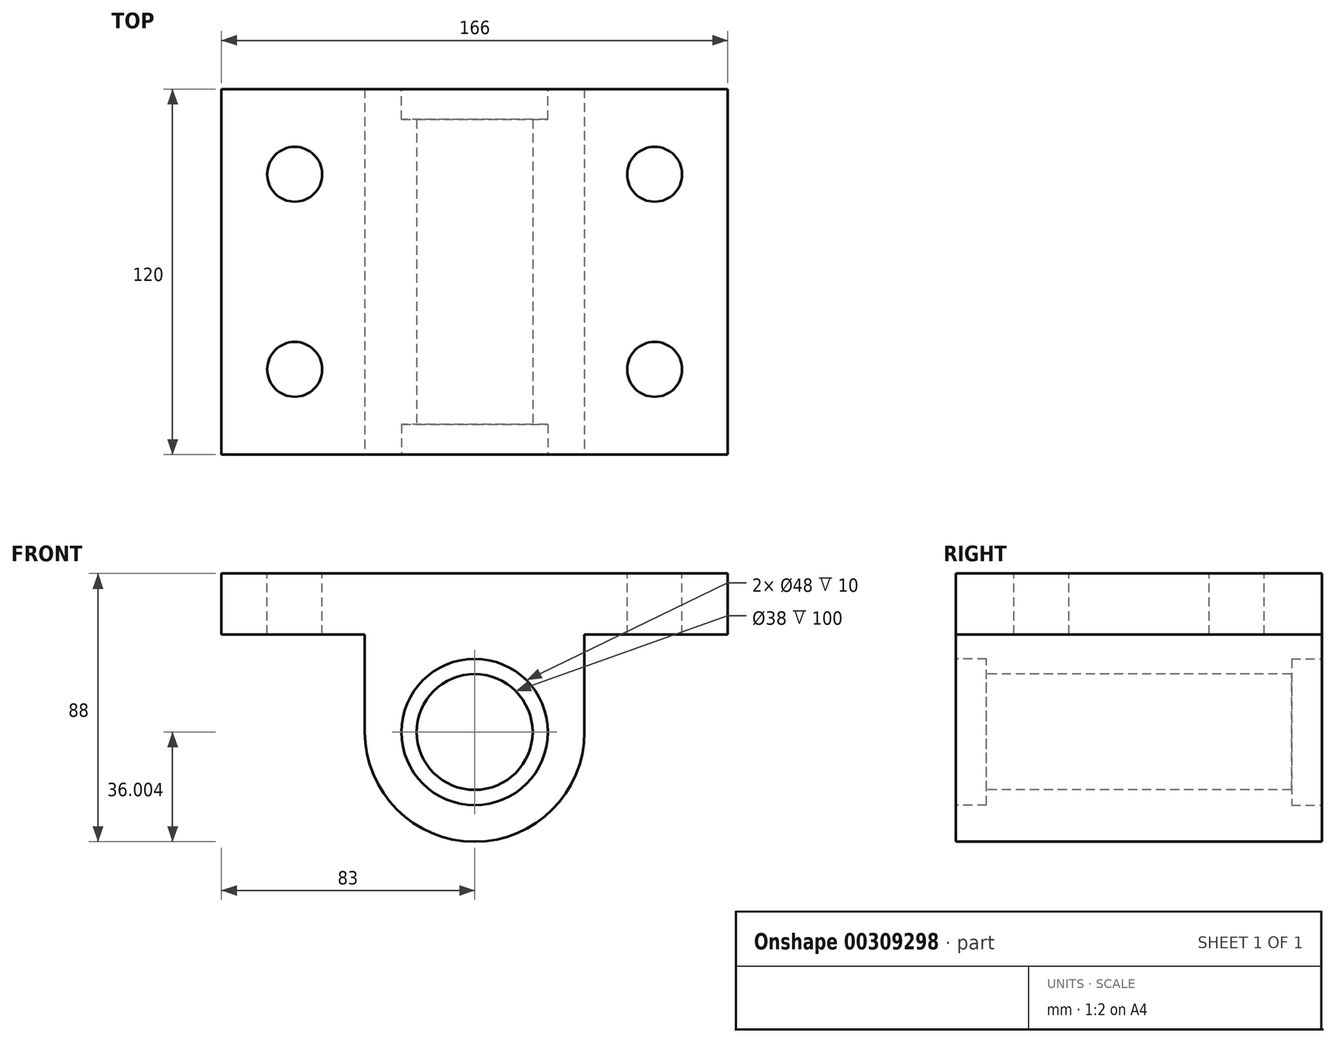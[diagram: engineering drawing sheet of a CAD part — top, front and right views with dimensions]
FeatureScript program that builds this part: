
annotation { "Feature Type Name" : "Feature", "Feature Type Description" : "" }
export const myFeature = defineFeature(function(context is Context, id is Id, definition is map)
    precondition{}
    {
        {
            var Q0;
            Q0=qCreatedBy(makeId("Front.planeOp"),FACE);
            var sketch = newSketch(context, id + "F0", { "sketchPlane" : qUnion([Q0])});
            skLineSegment(sketch, "E0.bottom", {"start": v(83, 33.32) * mm, "end": v(-83, 33.32) * mm});
            skLineSegment(sketch, "E0.top", {"start": v(83, 13.32) * mm, "end": v(36, 13.32) * mm});
            skLineSegment(sketch, "E0.left", {"start": v(83, 33.32) * mm, "end": v(83, 13.32) * mm});
            skLineSegment(sketch, "E0.right", {"start": v(-83, 33.32) * mm, "end": v(-83, 13.32) * mm});
            skPoint(sketch, "E0.middle", {"position": v(0, 23.32) * mm});
            skArc(sketch, "E1", {"start": v(-36, -18.68) * mm, "mid": v(0, -54.68) * mm, "end": v(36, -18.68) * mm});
            skCircle(sketch, "E2", {"center": v(0, -18.68) * mm, "radius": 24 * mm});
            skLineSegment(sketch, "E3", {"start": v(-36, 13.32) * mm, "end": v(-36, -18.68) * mm});
            skLineSegment(sketch, "E4", {"start": v(36, 13.32) * mm, "end": v(36, -18.68) * mm});
            skLineSegment(sketch, "E5.trimOffspring", {"start": v(-36, 13.32) * mm, "end": v(-83, 13.32) * mm});
            skCircle(sketch, "E6.0", {"center": v(0, -18.68) * mm, "radius": 19 * mm});
            skSolve(sketch);
        }
        {
            var Q0;
            Q0=makeQuery(id+"F0.imprint","IMPRINT",FACE,{"disambiguationData":[TD([[makeQuery(id+"F0.imprint","IMPRINT",EDGE,{"derivedFrom":sQuery(id+"F0.wireOp",EDGE,"E2")}),1.0]])]});
            var Q1;
            Q1=makeQuery(id+"F0.imprint","IMPRINT",FACE,{"disambiguationData":[TD([[makeQuery(id+"F0.imprint","IMPRINT",EDGE,{"derivedFrom":sQuery(id+"F0.wireOp",EDGE,"E0.bottom")}),1.0]])]});
            extrude(context, id + "F1", {"entities" : qUnion([Q0, Q1]), "endBound" : BoundingType.SYMMETRIC, "oppositeDirection" : true, "depth" : 120 * mm});
        }
        {
            var Q0;
            Q0=makeQuery(id+"F1.opExtrude","CAP_FACE",FACE,{"disambiguationData":[OSD([sQuery(id+"F0.wireOp",EDGE,"E0.bottom"),sQuery(id+"F0.wireOp",EDGE,"E0.top"),sQuery(id+"F0.wireOp",EDGE,"E0.left"),sQuery(id+"F0.wireOp",EDGE,"E0.right"),sQuery(id+"F0.wireOp",EDGE,"E1"),sQuery(id+"F0.wireOp",EDGE,"E3"),sQuery(id+"F0.wireOp",EDGE,"E4"),sQuery(id+"F0.wireOp",EDGE,"E5.trimOffspring"),sQuery(id+"F0.wireOp",EDGE,"E6.0")])],"isStart":true});
            var sketch = newSketch(context, id + "F2", { "sketchPlane" : qUnion([Q0])});
            skCircle(sketch, "E7", {"center": v(0, -18.68) * mm, "radius": 24 * mm});
            skSolve(sketch);
        }
        {
            var Q0;
            Q0=makeQuery(id+"F2.imprint","IMPRINT",FACE,{"disambiguationData":[TD([[makeQuery(id+"F2.imprint","IMPRINT",EDGE,{"derivedFrom":sQuery(id+"F2.wireOp",EDGE,"E7")}),1.0]])]});
            extrude(context, id + "F3", {"entities" : qUnion([Q0]), "operationType" : NewBodyOperationType.REMOVE, "oppositeDirection" : true, "depth" : 10 * mm});
        }
        {
            var Q0;
            Q0=makeQuery(id+"F1.opExtrude","CAP_FACE",FACE,{"disambiguationData":[OSD([sQuery(id+"F0.wireOp",EDGE,"E0.bottom"),sQuery(id+"F0.wireOp",EDGE,"E0.top"),sQuery(id+"F0.wireOp",EDGE,"E0.left"),sQuery(id+"F0.wireOp",EDGE,"E0.right"),sQuery(id+"F0.wireOp",EDGE,"E1"),sQuery(id+"F0.wireOp",EDGE,"E3"),sQuery(id+"F0.wireOp",EDGE,"E4"),sQuery(id+"F0.wireOp",EDGE,"E5.trimOffspring"),sQuery(id+"F0.wireOp",EDGE,"E6.0")])],"isStart":false});
            var sketch = newSketch(context, id + "F4", { "sketchPlane" : qUnion([Q0])});
            skCircle(sketch, "E8", {"center": v(0, -18.68) * mm, "radius": 24 * mm});
            skSolve(sketch);
        }
        {
            var Q0;
            Q0=makeQuery(id+"F4.imprint","IMPRINT",FACE,{"disambiguationData":[TD([[makeQuery(id+"F4.imprint","IMPRINT",EDGE,{"derivedFrom":sQuery(id+"F4.wireOp",EDGE,"E8")}),1.0]])]});
            extrude(context, id + "F5", {"entities" : qUnion([Q0]), "operationType" : NewBodyOperationType.REMOVE, "oppositeDirection" : true, "depth" : 10 * mm});
        }
        {
            var Q0;
            Q0=makeQuery(id+"F1.opExtrude","SWEPT_FACE",FACE,{"disambiguationData":[OSD([sQuery(id+"F0.wireOp",EDGE,"E0.bottom")])]});
            var sketch = newSketch(context, id + "F6", { "sketchPlane" : qUnion([Q0])});
            skCircle(sketch, "E9", {"center": v(-59, -32) * mm, "radius": 9 * mm});
            skCircle(sketch, "E10.0.1.0", {"center": v(-59, 32) * mm, "radius": 9 * mm});
            skCircle(sketch, "E10.1.0.0", {"center": v(59, -32) * mm, "radius": 9 * mm});
            skCircle(sketch, "E10.1.1.0", {"center": v(59, 32) * mm, "radius": 9 * mm});
            skLineSegment(sketch, "E10.direction1", {"start": v(-59, -32) * mm, "end": v(59, -32) * mm, "construction": true});
            skLineSegment(sketch, "E10.direction2", {"start": v(-59, -32) * mm, "end": v(-59, 32) * mm, "construction": true});
            skSolve(sketch);
        }
        {
            var Q0;
            Q0=makeQuery(id+"F6.imprint","IMPRINT",FACE,{"disambiguationData":[TD([[makeQuery(id+"F6.imprint","IMPRINT",EDGE,{"derivedFrom":sQuery(id+"F6.wireOp",EDGE,"E9")}),1.0]])]});
            var Q1;
            Q1=makeQuery(id+"F6.imprint","IMPRINT",FACE,{"disambiguationData":[TD([[makeQuery(id+"F6.imprint","IMPRINT",EDGE,{"derivedFrom":sQuery(id+"F6.wireOp",EDGE,"E10.0.1.0")}),1.0]])]});
            var Q2;
            Q2=makeQuery(id+"F6.imprint","IMPRINT",FACE,{"disambiguationData":[TD([[makeQuery(id+"F6.imprint","IMPRINT",EDGE,{"derivedFrom":sQuery(id+"F6.wireOp",EDGE,"E10.1.0.0")}),1.0]])]});
            var Q3;
            Q3=makeQuery(id+"F6.imprint","IMPRINT",FACE,{"disambiguationData":[TD([[makeQuery(id+"F6.imprint","IMPRINT",EDGE,{"derivedFrom":sQuery(id+"F6.wireOp",EDGE,"E10.1.1.0")}),1.0]])]});
            extrude(context, id + "F7", {"entities" : qUnion([Q0, Q1, Q2, Q3]), "operationType" : NewBodyOperationType.REMOVE, "oppositeDirection" : true, "depth" : 25 * mm});
        }
    });
